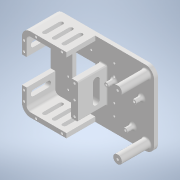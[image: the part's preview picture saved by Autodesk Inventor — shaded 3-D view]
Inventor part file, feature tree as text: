
AUTODESK INVENTOR PART (.ipt)
format: ipt  version: 2020 (Build 240168000, 168)  size: 395,776 bytes
history: native  units: mm
features: sketch x12, extrude x10, other x4, fillet x3, reference x2, hole x1, projected_geometry x1
ambient origin geometry x8: Origin, YZ Plane, XZ Plane, XY Plane, X Axis, Y Axis, Z Axis, Center Point
bodies: Solid1 (feature_tree)
feature tree (33):
  extrude  "Extrusion1"  Depth=130.0mm
  extrude  "Extrusion2"  Depth=15.0mm
  extrude  "Extrusion3"  Depth=15.0mm
  fillet  "Fillet1"  Radius=104.0mm
  extrude  "Extrusion4"  Depth=52.0mm
  extrude  "Extrusion5"  Depth=60.0mm
  sketch  "Sketch7"  dims[d17=7.5mm d18=30.0mm d19=50.0mm d20=0.0mm]
  extrude  "Extrusion6"  Depth=50.0mm
  fillet  "Fillet2"  Radius=50.0mm
  extrude  "Extrusion7"  Depth=40.0mm
  fillet  "Fillet3"  Radius=50.0mm
  hole  "Hole1"  [1 undecoded]
  extrude  "Extrusion8"  Depth=50.0mm TaperAngle=0.0deg
  extrude  "Extrusion9"  Depth=6.0mm
  extrude  "Extrusion10"  Depth=25.0mm
  sketch  "Sketch1"  dims[d0=180.0mm d1=130.0mm]
  sketch  "Sketch3"  dims[d2=7.0mm d3=0.0mm d9=15.0mm]
  sketch  "Sketch4"  dims[d10=15.0mm d11=15.0mm d12=104.0mm]
  sketch  "Sketch5"  dims[d13=52.0mm d14=75.0mm]
  projected_geometry  "Projected Loop1"
  sketch  "Sketch6"  dims[d15=12.0mm d16=60.0mm]
  sketch  "Sketch8"  dims[d21=46.0mm d22=40.0mm d23=50.0mm d24=0.0mm]
  reference  "Reference1"
  reference  "Reference2"
  sketch  "Sketch10"  dims[d25=28.0mm d26=2.0mm]
  sketch  "Sketch11"  dims[d27=8.0mm d28=50.0mm d29=0.0mm]
  sketch  "Sketch12"  dims[d30=4.0mm d31=6.0mm]
  sketch  "Sketch13"  dims[d32=25.0mm d33=25.0mm]
  sketch  "Sketch14"  dims[d34=45.0mm d35=3.5mm d36=8.0mm d37=3.5mm d38=17.0mm d39=6.0mm d40=6.0mm d41=3.5mm d42=17.0mm d43=3.5mm d44=10.0mm d45=0.0mm d46=10.0mm d47=0.0mm d48=2.0mm d49=7.0mm d50=13.0mm d51=0.0mm d52=4.0mm d53=4.0mm d54=6.0mm d55=6.3mm d56=2.0mm d57=90.0deg d58=5.0mm d59=20.594885mm d60=10.0mm d61=10.0mm d62=28.0mm d63=25.0mm d64=11.0mm d65=3.5mm d66=0.0mm d67=0.0mm d68=30.0mm d69=12.0mm d70=28.0mm d71=16.0mm d72=12.0mm d73=0.0mm d74=25.0mm d75=5.0mm d76=32.0mm d77=14.0mm d78=12.0mm d79=0.0mm]
  other  "<userpath>\Desktop\KangKangBalancing\KangKang.iam"
  other  "KangKang.iam"
  other  "Body-R:1"
  other  "bodyL:1"
note: 1 required parameter value undecoded (feature->parameter linkage not recoverable at this tier; creation-order binding heuristic only, values carry confidence <= 0.55)
